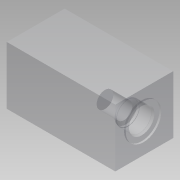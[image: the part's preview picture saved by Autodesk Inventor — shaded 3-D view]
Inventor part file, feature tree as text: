
AUTODESK INVENTOR PART (.ipt)
format: ipt  version: 2014 (Build 180170000, 170)  size: 159,744 bytes
history: native  units: mm
features: other x48, extrude x8, sketch x8
ambient origin geometry x8: Origin, YZ Plane, XZ Plane, XY Plane, X Axis, Y Axis, Z Axis, Center Point
bodies: 实体1 (feature_tree)
feature tree (64):
  extrude  "拉伸1"  Depth=49.0mm
  other  "UCS1"
  other  "UCS2"
  other  "UCS3"
  other  "UCS4"
  other  "UCS5"
  other  "UCS6"
  extrude  "拉伸2"  Depth=50.8mm
  extrude  "拉伸3"  Depth=2.5mm TaperAngle=0.0deg
  extrude  "拉伸5"  Depth=50.8mm
  extrude  "拉伸6"  Depth=50.8mm
  extrude  "拉伸7"  Depth=5.0mm
  extrude  "拉伸8"  Depth=50.8mm
  extrude  "拉伸9"  Depth=19.0mm TaperAngle=0.0deg
  sketch  "草图1"  dims[d0=80.0mm d1=0.0mm]
  sketch  "草图2"  dims[d2=0.0mm d3=0.0mm d4=0.0mm d5=0.0mm d6=0.0mm d7=0.0mm]
  sketch  "草图3"  dims[d8=0.0mm d9=0.0mm d10=0.0mm d11=0.0mm d12=0.0mm d13=0.0mm]
  sketch  "草图5"  dims[d14=0.0mm d15=0.0mm d16=0.0mm d17=0.0mm d18=0.0mm d19=0.0mm]
  sketch  "草图6"  dims[d20=0.0mm d21=0.0mm d22=0.0mm d23=0.0mm d24=0.0mm d25=0.0mm]
  sketch  "草图7"  dims[d26=0.0mm d27=0.0mm d28=0.0mm d29=0.0mm d30=0.0mm d31=0.0mm]
  sketch  "草图8"  dims[d32=0.0mm d33=0.0mm d34=0.0mm d35=0.0mm d36=0.0mm d37=0.0mm d38=49.0mm]
  sketch  "草图9"  dims[d39=39.0mm d40=40.0mm d41=2.5mm d42=0.0mm d43=35.1mm d44=3.1mm d45=-2.617994mm d49=5.0mm d50=-7.853982mm d51=33.0mm d52=19.0mm d53=0.0mm d54=31.0mm d55=22.0mm d56=0.0mm d57=22.0mm d58=-10.471976mm d59=23.0mm d60=50.8mm d61=0.0mm]
  other  "UCS1: YZ 平面"
  other  "UCS1: XZ 平面"
  other  "UCS1: XY 平面"
  other  "UCS1: X 轴"
  other  "UCS1: Y 轴"
  other  "UCS1: Z 轴"
  other  "UCS1: 原点"
  other  "UCS2: YZ 平面"
  other  "UCS2: XZ 平面"
  other  "UCS2: XY 平面"
  other  "UCS2: X 轴"
  other  "UCS2: Y 轴"
  other  "UCS2: Z 轴"
  other  "UCS2: 原点"
  other  "UCS3: YZ 平面"
  other  "UCS3: XZ 平面"
  other  "UCS3: XY 平面"
  other  "UCS3: X 轴"
  other  "UCS3: Y 轴"
  other  "UCS3: Z 轴"
  other  "UCS3: 原点"
  other  "UCS4: YZ 平面"
  other  "UCS4: XZ 平面"
  other  "UCS4: XY 平面"
  other  "UCS4: X 轴"
  other  "UCS4: Y 轴"
  other  "UCS4: Z 轴"
  other  "UCS4: 原点"
  other  "UCS5: YZ 平面"
  other  "UCS5: XZ 平面"
  other  "UCS5: XY 平面"
  other  "UCS5: X 轴"
  other  "UCS5: Y 轴"
  other  "UCS5: Z 轴"
  other  "UCS5: 原点"
  other  "UCS6: YZ 平面"
  other  "UCS6: XZ 平面"
  other  "UCS6: XY 平面"
  other  "UCS6: X 轴"
  other  "UCS6: Y 轴"
  other  "UCS6: Z 轴"
  other  "UCS6: 原点"
